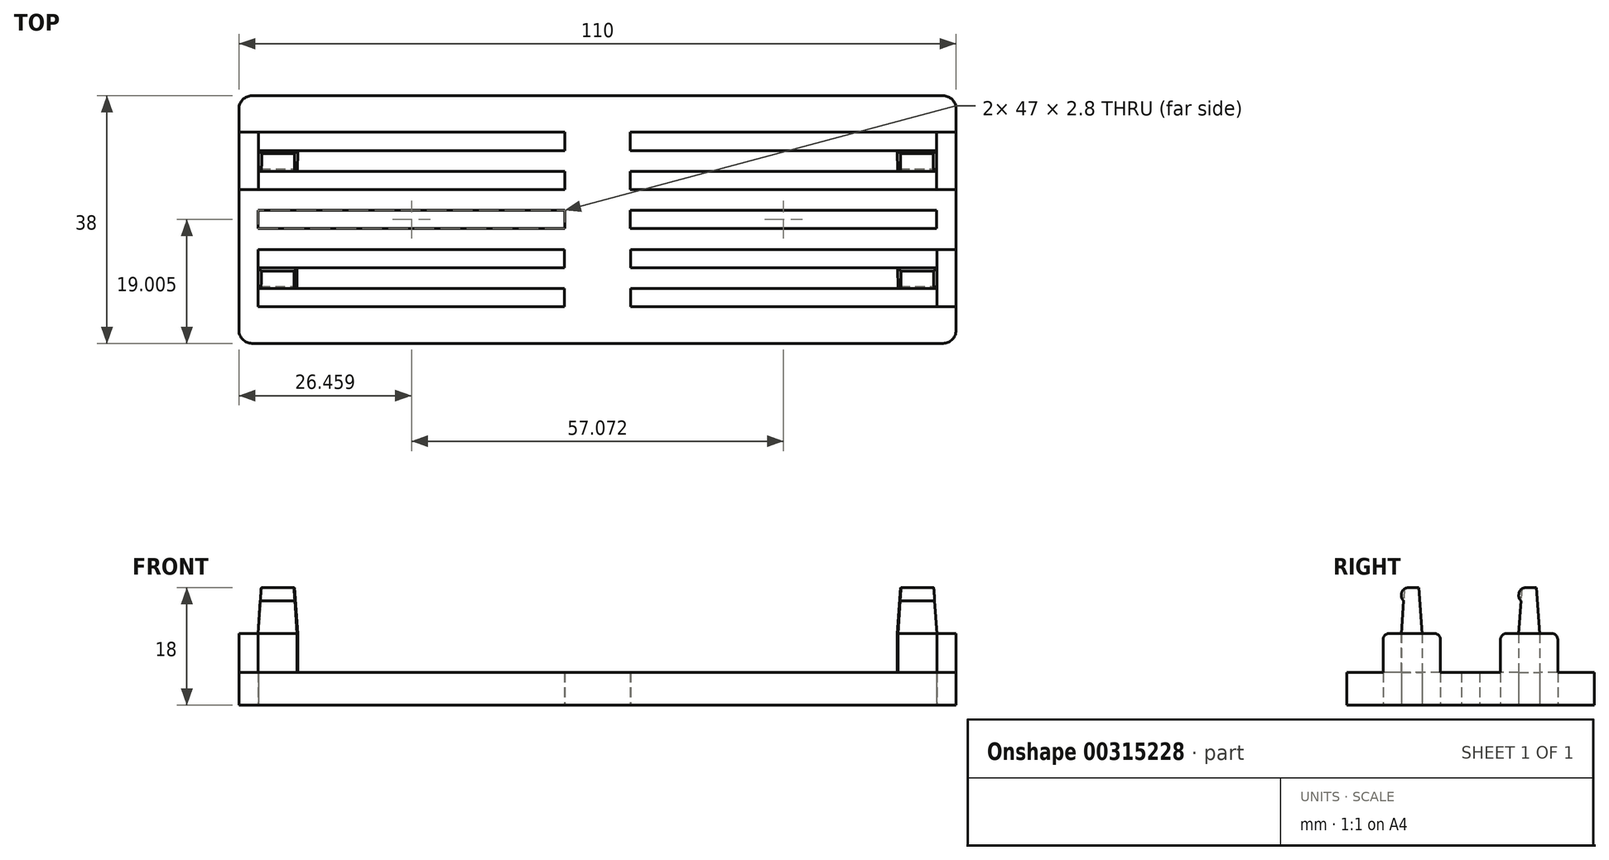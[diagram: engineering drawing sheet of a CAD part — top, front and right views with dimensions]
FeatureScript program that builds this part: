
annotation { "Feature Type Name" : "Feature", "Feature Type Description" : "" }
export const myFeature = defineFeature(function(context is Context, id is Id, definition is map)
    precondition{}
    {
        {
            var Q0;
            Q0=qCreatedBy(makeId("Top.planeOp"),FACE);
            var sketch = newSketch(context, id + "F0", { "sketchPlane" : qUnion([Q0])});
            skLineSegment(sketch, "E0.bottom", {"start": v(-62.65, 12.42) * mm, "end": v(47.35, 12.42) * mm});
            skLineSegment(sketch, "E0.top", {"start": v(-62.65, -25.58) * mm, "end": v(47.35, -25.58) * mm});
            skLineSegment(sketch, "E0.left", {"start": v(-62.65, 12.42) * mm, "end": v(-62.65, -25.58) * mm});
            skLineSegment(sketch, "E0.right", {"start": v(47.35, 12.42) * mm, "end": v(47.35, -25.58) * mm});
            skPoint(sketch, "E1", {"position": v(-7.65, 12.42) * mm});
            skLineSegment(sketch, "E2.bottom", {"start": v(-59.65, 6.82) * mm, "end": v(-12.65, 6.82) * mm});
            skLineSegment(sketch, "E2.top", {"start": v(-59.65, 4.02) * mm, "end": v(-12.65, 4.02) * mm});
            skLineSegment(sketch, "E2.left", {"start": v(-59.65, 6.82) * mm, "end": v(-59.65, 4.02) * mm});
            skLineSegment(sketch, "E2.right", {"start": v(-12.65, 6.82) * mm, "end": v(-12.65, 4.02) * mm});
            skLineSegment(sketch, "E3.1.0.0", {"start": v(-59.67, 0.82) * mm, "end": v(-59.67, -1.98) * mm});
            skLineSegment(sketch, "E3.1.0.1", {"start": v(-59.67, 0.82) * mm, "end": v(-12.67, 0.82) * mm});
            skLineSegment(sketch, "E3.1.0.2", {"start": v(-59.67, -1.98) * mm, "end": v(-12.67, -1.98) * mm});
            skLineSegment(sketch, "E3.1.0.3", {"start": v(-12.67, 0.82) * mm, "end": v(-12.67, -1.98) * mm});
            skLineSegment(sketch, "E3.2.0.0", {"start": v(-59.7, -5.18) * mm, "end": v(-59.7, -7.98) * mm});
            skLineSegment(sketch, "E3.2.0.1", {"start": v(-59.7, -5.18) * mm, "end": v(-12.7, -5.18) * mm});
            skLineSegment(sketch, "E3.2.0.2", {"start": v(-59.7, -7.98) * mm, "end": v(-12.7, -7.98) * mm});
            skLineSegment(sketch, "E3.2.0.3", {"start": v(-12.7, -5.18) * mm, "end": v(-12.7, -7.98) * mm});
            skLineSegment(sketch, "E3.3.0.0", {"start": v(-59.7, -11.17) * mm, "end": v(-59.7, -13.97) * mm});
            skLineSegment(sketch, "E3.3.0.1", {"start": v(-59.7, -11.17) * mm, "end": v(-12.7, -11.17) * mm});
            skLineSegment(sketch, "E3.3.0.2", {"start": v(-59.7, -13.97) * mm, "end": v(-12.7, -13.97) * mm});
            skLineSegment(sketch, "E3.3.0.3", {"start": v(-12.7, -11.17) * mm, "end": v(-12.7, -13.97) * mm});
            skLineSegment(sketch, "E3.4.0.0", {"start": v(-59.73, -17.17) * mm, "end": v(-59.73, -19.97) * mm});
            skLineSegment(sketch, "E3.4.0.1", {"start": v(-59.73, -17.17) * mm, "end": v(-12.73, -17.17) * mm});
            skLineSegment(sketch, "E3.4.0.2", {"start": v(-59.73, -19.97) * mm, "end": v(-12.73, -19.97) * mm});
            skLineSegment(sketch, "E3.4.0.3", {"start": v(-12.73, -17.17) * mm, "end": v(-12.73, -19.97) * mm});
            skLineSegment(sketch, "E3.direction1", {"start": v(-59.65, 4.02) * mm, "end": v(-59.67, -1.98) * mm, "construction": true});
            skPoint(sketch, "E4", {"position": v(-7.65, -25.58) * mm});
            skLineSegment(sketch, "E5.MirrorCS", {"start": v(44.4, -11.17) * mm, "end": v(44.4, -13.97) * mm});
            skLineSegment(sketch, "E6.MirrorCS", {"start": v(-2.6, -11.17) * mm, "end": v(-2.6, -13.97) * mm});
            skLineSegment(sketch, "E7.MirrorCS", {"start": v(-2.62, -5.18) * mm, "end": v(-2.62, -7.98) * mm});
            skLineSegment(sketch, "E8.MirrorCS", {"start": v(44.35, 6.82) * mm, "end": v(44.35, 4.02) * mm});
            skLineSegment(sketch, "E9.MirrorCS", {"start": v(44.36, 0.82) * mm, "end": v(44.36, -1.98) * mm});
            skLineSegment(sketch, "E10.MirrorCS", {"start": v(-2.64, 0.82) * mm, "end": v(-2.64, -1.98) * mm});
            skLineSegment(sketch, "E11.MirrorCS", {"start": v(44.38, -5.18) * mm, "end": v(44.38, -7.98) * mm});
            skLineSegment(sketch, "E12.MirrorCS", {"start": v(-2.65, 6.82) * mm, "end": v(-2.65, 4.02) * mm});
            skLineSegment(sketch, "E13.MirrorCS", {"start": v(-2.58, -17.17) * mm, "end": v(-2.58, -19.97) * mm});
            skLineSegment(sketch, "E14.MirrorCS", {"start": v(44.42, -17.17) * mm, "end": v(44.42, -19.97) * mm});
            skLineSegment(sketch, "E15.MirrorCS", {"start": v(44.42, -17.17) * mm, "end": v(-2.58, -17.17) * mm});
            skLineSegment(sketch, "E16.MirrorCS", {"start": v(44.35, 4.02) * mm, "end": v(44.36, -1.98) * mm, "construction": true});
            skLineSegment(sketch, "E17.MirrorCS", {"start": v(44.38, -5.18) * mm, "end": v(-2.62, -5.18) * mm});
            skLineSegment(sketch, "E18.MirrorCS", {"start": v(44.4, -11.17) * mm, "end": v(-2.6, -11.17) * mm});
            skLineSegment(sketch, "E19.MirrorCS", {"start": v(44.38, -7.98) * mm, "end": v(-2.62, -7.98) * mm});
            skLineSegment(sketch, "E20.MirrorCS", {"start": v(44.35, 6.82) * mm, "end": v(-2.65, 6.82) * mm});
            skLineSegment(sketch, "E21.MirrorCS", {"start": v(44.35, 4.02) * mm, "end": v(-2.65, 4.02) * mm});
            skLineSegment(sketch, "E22.MirrorCS", {"start": v(44.36, 0.82) * mm, "end": v(-2.64, 0.82) * mm});
            skLineSegment(sketch, "E23.MirrorCS", {"start": v(44.36, -1.98) * mm, "end": v(-2.64, -1.98) * mm});
            skLineSegment(sketch, "E24.MirrorCS", {"start": v(44.42, -19.97) * mm, "end": v(-2.58, -19.97) * mm});
            skLineSegment(sketch, "E25.MirrorCS", {"start": v(44.4, -13.97) * mm, "end": v(-2.6, -13.97) * mm});
            skSolve(sketch);
        }
        {
            var Q0;
            Q0=makeQuery(id+"F0.imprint","IMPRINT",FACE,{"disambiguationData":[TD([[makeQuery(id+"F0.imprint","IMPRINT",EDGE,{"derivedFrom":sQuery(id+"F0.wireOp",EDGE,"E0.bottom")}),-1.0]])]});
            extrude(context, id + "F1", {"entities" : qUnion([Q0]), "depth" : 5 * mm});
        }
        {
            var Q0;
            Q0=makeQuery(id+"F1.opExtrude","SWEPT_EDGE",EDGE,{"disambiguationData":[OSD([sQuery(id+"F0.wireOp",EDGE,"E0.bottom"),sQuery(id+"F0.wireOp",EDGE,"E0.left")])]});
            var Q1;
            Q1=makeQuery(id+"F1.opExtrude","SWEPT_EDGE",EDGE,{"disambiguationData":[OSD([sQuery(id+"F0.wireOp",EDGE,"E0.top"),sQuery(id+"F0.wireOp",EDGE,"E0.left")])]});
            var Q2;
            Q2=makeQuery(id+"F1.opExtrude","SWEPT_EDGE",EDGE,{"disambiguationData":[OSD([sQuery(id+"F0.wireOp",EDGE,"E0.bottom"),sQuery(id+"F0.wireOp",EDGE,"E0.right")])]});
            var Q3;
            Q3=makeQuery(id+"F1.opExtrude","SWEPT_EDGE",EDGE,{"disambiguationData":[OSD([sQuery(id+"F0.wireOp",EDGE,"E0.top"),sQuery(id+"F0.wireOp",EDGE,"E0.right")])]});
            fillet(context, id + "F2", {"entities" : qUnion([Q0, Q1, Q2, Q3]), "radius" : 2 * mm, "tangentPropagation" : true, "allowEdgeOverflow" : false});
        }
        {
            var Q0;
            Q0=makeQuery(id+"F1.opExtrude","CAP_FACE",FACE,{"disambiguationData":[OSD([sQuery(id+"F0.wireOp",EDGE,"E0.bottom"),sQuery(id+"F0.wireOp",EDGE,"E0.top"),sQuery(id+"F0.wireOp",EDGE,"E0.left"),sQuery(id+"F0.wireOp",EDGE,"E0.right"),sQuery(id+"F0.wireOp",EDGE,"E2.bottom"),sQuery(id+"F0.wireOp",EDGE,"E2.top"),sQuery(id+"F0.wireOp",EDGE,"E2.left"),sQuery(id+"F0.wireOp",EDGE,"E2.right"),sQuery(id+"F0.wireOp",EDGE,"E3.1.0.0"),sQuery(id+"F0.wireOp",EDGE,"E3.1.0.1"),sQuery(id+"F0.wireOp",EDGE,"E3.1.0.2"),sQuery(id+"F0.wireOp",EDGE,"E3.1.0.3"),sQuery(id+"F0.wireOp",EDGE,"E3.2.0.0"),sQuery(id+"F0.wireOp",EDGE,"E3.2.0.1"),sQuery(id+"F0.wireOp",EDGE,"E3.2.0.2"),sQuery(id+"F0.wireOp",EDGE,"E3.2.0.3"),sQuery(id+"F0.wireOp",EDGE,"E3.3.0.0"),sQuery(id+"F0.wireOp",EDGE,"E3.3.0.1"),sQuery(id+"F0.wireOp",EDGE,"E3.3.0.2"),sQuery(id+"F0.wireOp",EDGE,"E3.3.0.3"),sQuery(id+"F0.wireOp",EDGE,"E3.4.0.0"),sQuery(id+"F0.wireOp",EDGE,"E3.4.0.1"),sQuery(id+"F0.wireOp",EDGE,"E3.4.0.2"),sQuery(id+"F0.wireOp",EDGE,"E3.4.0.3"),sQuery(id+"F0.wireOp",EDGE,"E5.MirrorCS"),sQuery(id+"F0.wireOp",EDGE,"E6.MirrorCS"),sQuery(id+"F0.wireOp",EDGE,"E7.MirrorCS"),sQuery(id+"F0.wireOp",EDGE,"E8.MirrorCS"),sQuery(id+"F0.wireOp",EDGE,"E9.MirrorCS"),sQuery(id+"F0.wireOp",EDGE,"E10.MirrorCS"),sQuery(id+"F0.wireOp",EDGE,"E11.MirrorCS"),sQuery(id+"F0.wireOp",EDGE,"E12.MirrorCS"),sQuery(id+"F0.wireOp",EDGE,"E13.MirrorCS"),sQuery(id+"F0.wireOp",EDGE,"E14.MirrorCS"),sQuery(id+"F0.wireOp",EDGE,"E15.MirrorCS"),sQuery(id+"F0.wireOp",EDGE,"E17.MirrorCS"),sQuery(id+"F0.wireOp",EDGE,"E18.MirrorCS"),sQuery(id+"F0.wireOp",EDGE,"E19.MirrorCS"),sQuery(id+"F0.wireOp",EDGE,"E20.MirrorCS"),sQuery(id+"F0.wireOp",EDGE,"E21.MirrorCS"),sQuery(id+"F0.wireOp",EDGE,"E22.MirrorCS"),sQuery(id+"F0.wireOp",EDGE,"E23.MirrorCS"),sQuery(id+"F0.wireOp",EDGE,"E24.MirrorCS"),sQuery(id+"F0.wireOp",EDGE,"E25.MirrorCS")])],"isStart":false});
            var sketch = newSketch(context, id + "F3", { "sketchPlane" : qUnion([Q0])});
            skLineSegment(sketch, "E26", {"start": v(-59.65, 6.82) * mm, "end": v(-62.65, 6.82) * mm});
            skLineSegment(sketch, "E27", {"start": v(-59.67, -1.98) * mm, "end": v(-62.65, -1.98) * mm});
            skLineSegment(sketch, "E28", {"start": v(-59.67, 0.82) * mm, "end": v(-59.65, 4.02) * mm});
            skLineSegment(sketch, "E29.1.0.0", {"start": v(-53.67, 0.82) * mm, "end": v(-53.65, 4.02) * mm});
            skLineSegment(sketch, "E30.1.0.1", {"start": v(-53.74, -17.17) * mm, "end": v(-53.72, -13.97) * mm});
            skLineSegment(sketch, "E30.1.0.2", {"start": v(-59.74, -17.17) * mm, "end": v(-59.72, -13.97) * mm});
            skLineSegment(sketch, "E30.1.0.3", {"start": v(-59.74, -19.97) * mm, "end": v(-62.72, -19.97) * mm});
            skLineSegment(sketch, "E30.1.0.4", {"start": v(-59.72, -11.17) * mm, "end": v(-62.72, -11.17) * mm});
            skPoint(sketch, "E31", {"position": v(-7.65, 12.42) * mm});
            skPoint(sketch, "E32", {"position": v(-7.65, -25.58) * mm});
            skLineSegment(sketch, "E33", {"start": v(-7.65, 12.42) * mm, "end": v(-7.65, -25.58) * mm});
            skLineSegment(sketch, "E34.MirrorCS", {"start": v(44.35, 6.82) * mm, "end": v(47.35, 6.82) * mm});
            skLineSegment(sketch, "E35.MirrorCS", {"start": v(44.36, -1.98) * mm, "end": v(47.35, -1.98) * mm});
            skLineSegment(sketch, "E36.MirrorCS", {"start": v(44.36, 0.82) * mm, "end": v(44.35, 4.02) * mm});
            skLineSegment(sketch, "E37.MirrorCS", {"start": v(38.36, 0.82) * mm, "end": v(38.35, 4.02) * mm});
            skLineSegment(sketch, "E38.MirrorCS", {"start": v(38.43, -17.17) * mm, "end": v(38.4, -13.97) * mm});
            skLineSegment(sketch, "E39", {"start": v(-59.73, -17.17) * mm, "end": v(-59.7, -13.97) * mm});
            skLineSegment(sketch, "E40", {"start": v(-62.72, -11.17) * mm, "end": v(-59.7, -11.17) * mm});
            skLineSegment(sketch, "E41", {"start": v(-62.72, -19.97) * mm, "end": v(-59.73, -19.97) * mm});
            skLineSegment(sketch, "E42", {"start": v(44.4, -11.17) * mm, "end": v(47.35, -11.17) * mm});
            skLineSegment(sketch, "E43", {"start": v(44.42, -19.97) * mm, "end": v(47.35, -19.97) * mm});
            skLineSegment(sketch, "E44", {"start": v(44.42, -17.17) * mm, "end": v(44.4, -13.97) * mm});
            skSolve(sketch);
        }
        {
            var Q0;
            {var subQ0=sQuery(id+"F3.wireOp",EDGE,"E26");Q0=makeQuery(id+"F3.imprint","IMPRINT",FACE,{"disambiguationData":[TD([[makeQuery(id+"F3.imprint","IMPRINT",EDGE,{"derivedFrom":subQ0}),1.0]])]});}
            var Q1;
            {var subQ0=sQuery(id+"F3.wireOp",EDGE,"E28");Q1=makeQuery(id+"F3.imprint","IMPRINT",FACE,{"disambiguationData":[TD([[makeQuery(id+"F3.imprint","IMPRINT",EDGE,{"derivedFrom":subQ0}),-1.0]])]});}
            var Q2;
            {var subQ0=sQuery(id+"F3.wireOp",EDGE,"E30.1.0.1");Q2=makeQuery(id+"F3.imprint","IMPRINT",FACE,{"disambiguationData":[TD([[makeQuery(id+"F3.imprint","IMPRINT",EDGE,{"derivedFrom":subQ0}),1.0]])]});}
            var Q3;
            {var subQ4=sQuery(id+"F3.wireOp",EDGE,"E30.1.0.3");Q3=makeQuery(id+"F3.imprint","IMPRINT",FACE,{"disambiguationData":[TD([[makeQuery(id+"F3.imprint","IMPRINT",EDGE,{"derivedFrom":subQ4}),-1.0]])]});}
            var Q4;
            {var subQ0=sQuery(id+"F3.wireOp",EDGE,"E38.MirrorCS");Q4=makeQuery(id+"F3.imprint","IMPRINT",FACE,{"disambiguationData":[TD([[makeQuery(id+"F3.imprint","IMPRINT",EDGE,{"derivedFrom":subQ0}),-1.0]])]});}
            var Q5;
            {var subQ0=sQuery(id+"F3.wireOp",EDGE,"E42");Q5=makeQuery(id+"F3.imprint","IMPRINT",FACE,{"disambiguationData":[TD([[makeQuery(id+"F3.imprint","IMPRINT",EDGE,{"derivedFrom":subQ0}),-1.0]])]});}
            var Q6;
            {var subQ0=sQuery(id+"F3.wireOp",EDGE,"E36.MirrorCS");Q6=makeQuery(id+"F3.imprint","IMPRINT",FACE,{"disambiguationData":[TD([[makeQuery(id+"F3.imprint","IMPRINT",EDGE,{"derivedFrom":subQ0}),1.0]])]});}
            var Q7;
            {var subQ0=sQuery(id+"F3.wireOp",EDGE,"E34.MirrorCS");Q7=makeQuery(id+"F3.imprint","IMPRINT",FACE,{"disambiguationData":[TD([[makeQuery(id+"F3.imprint","IMPRINT",EDGE,{"derivedFrom":subQ0}),-1.0]])]});}
            extrude(context, id + "F4", {"entities" : qUnion([Q0, Q1, Q2, Q3, Q4, Q5, Q6, Q7]), "operationType" : NewBodyOperationType.ADD, "depth" : 6 * mm});
        }
        {
            var Q0;
            Q0=makeQuery(id+"F4.opExtrude","CAP_EDGE",EDGE,{"disambiguationData":[OSD([sQuery(id+"F3.wireOp",EDGE,"E26")])],"isStart":false});
            var Q1;
            Q1=makeQuery(id+"F4.opExtrude","CAP_EDGE",EDGE,{"disambiguationData":[OSD([sQuery(id+"F3.wireOp",EDGE,"E27")])],"isStart":false});
            var Q2;
            Q2=makeQuery(id+"F4.opExtrude","CAP_EDGE",EDGE,{"disambiguationData":[OSD([sQuery(id+"F3.wireOp",EDGE,"E40")])],"isStart":false});
            var Q3;
            Q3=makeQuery(id+"F4.opExtrude","CAP_EDGE",EDGE,{"disambiguationData":[OSD([sQuery(id+"F3.wireOp",EDGE,"E30.1.0.3")])],"isStart":false});
            var Q4;
            Q4=makeQuery(id+"F4.opExtrude","CAP_EDGE",EDGE,{"disambiguationData":[OSD([sQuery(id+"F3.wireOp",EDGE,"E43")])],"isStart":false});
            var Q5;
            Q5=makeQuery(id+"F4.opExtrude","CAP_EDGE",EDGE,{"disambiguationData":[OSD([sQuery(id+"F3.wireOp",EDGE,"E42")])],"isStart":false});
            var Q6;
            Q6=makeQuery(id+"F4.opExtrude","CAP_EDGE",EDGE,{"disambiguationData":[OSD([sQuery(id+"F3.wireOp",EDGE,"E35.MirrorCS")])],"isStart":false});
            var Q7;
            Q7=makeQuery(id+"F4.opExtrude","CAP_EDGE",EDGE,{"disambiguationData":[OSD([sQuery(id+"F3.wireOp",EDGE,"E34.MirrorCS")])],"isStart":false});
            var Q8;
            Q8=makeQuery(id+"F4.opExtrude","CAP_EDGE",EDGE,{"disambiguationData":[OSD([sQuery(id+"F3.wireOp",EDGE,"E26")])],"isStart":true});
            var Q9;
            Q9=makeQuery(id+"F4.opExtrude","CAP_EDGE",EDGE,{"disambiguationData":[OSD([sQuery(id+"F3.wireOp",EDGE,"E40")])],"isStart":true});
            var Q10;
            Q10=makeQuery(id+"F4.opExtrude","CAP_EDGE",EDGE,{"disambiguationData":[OSD([sQuery(id+"F3.wireOp",EDGE,"E42")])],"isStart":true});
            var Q11;
            Q11=makeQuery(id+"F4.opExtrude","CAP_EDGE",EDGE,{"disambiguationData":[OSD([sQuery(id+"F3.wireOp",EDGE,"E34.MirrorCS")])],"isStart":true});
            var Q12;
            Q12=makeQuery(id+"F4.opExtrude","CAP_EDGE",EDGE,{"disambiguationData":[OSD([sQuery(id+"F3.wireOp",EDGE,"E37.MirrorCS")])],"isStart":true});
            var Q13;
            Q13=makeQuery(id+"F4.opExtrude","CAP_EDGE",EDGE,{"disambiguationData":[OSD([sQuery(id+"F3.wireOp",EDGE,"E38.MirrorCS")])],"isStart":true});
            var Q14;
            Q14=makeQuery(id+"F4.opExtrude","CAP_EDGE",EDGE,{"disambiguationData":[OSD([sQuery(id+"F3.wireOp",EDGE,"E29.1.0.0")])],"isStart":true});
            var Q15;
            Q15=makeQuery(id+"F4.opExtrude","CAP_EDGE",EDGE,{"disambiguationData":[OSD([sQuery(id+"F3.wireOp",EDGE,"E27")])],"isStart":true});
            var Q16;
            Q16=makeQuery(id+"F4.opExtrude","CAP_EDGE",EDGE,{"disambiguationData":[OSD([sQuery(id+"F3.wireOp",EDGE,"E30.1.0.1")])],"isStart":true});
            var Q17;
            Q17=makeQuery(id+"F4.opExtrude","CAP_EDGE",EDGE,{"disambiguationData":[OSD([sQuery(id+"F3.wireOp",EDGE,"E30.1.0.3")])],"isStart":true});
            var Q18;
            Q18=makeQuery(id+"F4.opExtrude","CAP_EDGE",EDGE,{"disambiguationData":[OSD([sQuery(id+"F3.wireOp",EDGE,"E43")])],"isStart":true});
            var Q19;
            Q19=makeQuery(id+"F4.opExtrude","CAP_EDGE",EDGE,{"disambiguationData":[OSD([sQuery(id+"F3.wireOp",EDGE,"E35.MirrorCS")])],"isStart":true});
            fillet(context, id + "F5", {"entities" : qUnion([Q0, Q1, Q2, Q3, Q4, Q5, Q6, Q7, Q8, Q9, Q10, Q11, Q12, Q13, Q14, Q15, Q16, Q17, Q18, Q19]), "radius" : 1 * mm, "tangentPropagation" : true, "allowEdgeOverflow" : false});
        }
        {
            var Q0;
            Q0=makeQuery(id+"F4.opExtrude","CAP_FACE",FACE,{"disambiguationData":[OSD([sQuery(id+"F0.wireOp",EDGE,"E0.left"),sQuery(id+"F0.wireOp",EDGE,"E2.top"),sQuery(id+"F0.wireOp",EDGE,"E2.left"),sQuery(id+"F0.wireOp",EDGE,"E3.1.0.0"),sQuery(id+"F0.wireOp",EDGE,"E3.1.0.1"),sQuery(id+"F3.wireOp",EDGE,"E26"),sQuery(id+"F3.wireOp",EDGE,"E27"),sQuery(id+"F3.wireOp",EDGE,"E29.1.0.0")])],"isStart":false});
            var sketch = newSketch(context, id + "F6", { "sketchPlane" : qUnion([Q0])});
            skLineSegment(sketch, "E45", {"start": v(-59.67, 0.82) * mm, "end": v(-59.65, 4.02) * mm});
            skSolve(sketch);
        }
        {
            var Q0;
            Q0=makeQuery(id+"F4.opExtrude","CAP_FACE",FACE,{"disambiguationData":[OSD([sQuery(id+"F0.wireOp",EDGE,"E0.left"),sQuery(id+"F0.wireOp",EDGE,"E3.3.0.0"),sQuery(id+"F0.wireOp",EDGE,"E3.3.0.2"),sQuery(id+"F0.wireOp",EDGE,"E3.4.0.0"),sQuery(id+"F0.wireOp",EDGE,"E3.4.0.1"),sQuery(id+"F3.wireOp",EDGE,"E30.1.0.3"),sQuery(id+"F3.wireOp",EDGE,"E30.1.0.1"),sQuery(id+"F3.wireOp",EDGE,"E40"),sQuery(id+"F3.wireOp",EDGE,"E41")])],"isStart":false});
            var sketch = newSketch(context, id + "F7", { "sketchPlane" : qUnion([Q0])});
            skLineSegment(sketch, "E46", {"start": v(-59.73, -17.17) * mm, "end": v(-59.7, -13.97) * mm});
            skSolve(sketch);
        }
        {
            var Q0;
            Q0=makeQuery(id+"F4.opExtrude","CAP_FACE",FACE,{"disambiguationData":[OSD([sQuery(id+"F0.wireOp",EDGE,"E0.right"),sQuery(id+"F0.wireOp",EDGE,"E8.MirrorCS"),sQuery(id+"F0.wireOp",EDGE,"E9.MirrorCS"),sQuery(id+"F0.wireOp",EDGE,"E21.MirrorCS"),sQuery(id+"F0.wireOp",EDGE,"E22.MirrorCS"),sQuery(id+"F3.wireOp",EDGE,"E34.MirrorCS"),sQuery(id+"F3.wireOp",EDGE,"E35.MirrorCS"),sQuery(id+"F3.wireOp",EDGE,"E37.MirrorCS")])],"isStart":false});
            var sketch = newSketch(context, id + "F8", { "sketchPlane" : qUnion([Q0])});
            skLineSegment(sketch, "E47", {"start": v(44.36, 0.82) * mm, "end": v(44.35, 4.02) * mm});
            skSolve(sketch);
        }
        {
            var Q0;
            Q0=makeQuery(id+"F4.opExtrude","CAP_FACE",FACE,{"disambiguationData":[OSD([sQuery(id+"F0.wireOp",EDGE,"E0.right"),sQuery(id+"F0.wireOp",EDGE,"E5.MirrorCS"),sQuery(id+"F0.wireOp",EDGE,"E14.MirrorCS"),sQuery(id+"F0.wireOp",EDGE,"E15.MirrorCS"),sQuery(id+"F0.wireOp",EDGE,"E25.MirrorCS"),sQuery(id+"F3.wireOp",EDGE,"E38.MirrorCS"),sQuery(id+"F3.wireOp",EDGE,"E42"),sQuery(id+"F3.wireOp",EDGE,"E43")])],"isStart":false});
            var sketch = newSketch(context, id + "F9", { "sketchPlane" : qUnion([Q0])});
            skLineSegment(sketch, "E48", {"start": v(44.42, -17.17) * mm, "end": v(44.4, -13.97) * mm});
            skSolve(sketch);
        }
        {
            var Q0;
            Q0=makeQuery(id+"F6.imprint","IMPRINT",FACE,{"disambiguationData":[TD([[makeQuery(id+"F6.imprint","IMPRINT",EDGE,{"derivedFrom":sQuery(id+"F6.wireOp",EDGE,"E45")}),-1.0]])]});
            var Q1;
            Q1=makeQuery(id+"F7.imprint","IMPRINT",FACE,{"disambiguationData":[TD([[makeQuery(id+"F7.imprint","IMPRINT",EDGE,{"derivedFrom":sQuery(id+"F7.wireOp",EDGE,"E46")}),-1.0]])]});
            var Q2;
            Q2=makeQuery(id+"F9.imprint","IMPRINT",FACE,{"disambiguationData":[TD([[makeQuery(id+"F9.imprint","IMPRINT",EDGE,{"derivedFrom":sQuery(id+"F9.wireOp",EDGE,"E48")}),1.0]])]});
            var Q3;
            Q3=makeQuery(id+"F8.imprint","IMPRINT",FACE,{"disambiguationData":[TD([[makeQuery(id+"F8.imprint","IMPRINT",EDGE,{"derivedFrom":sQuery(id+"F8.wireOp",EDGE,"E47")}),1.0]])]});
            extrude(context, id + "F10", {"entities" : qUnion([Q0, Q1, Q2, Q3]), "operationType" : NewBodyOperationType.ADD, "depth" : 7 * mm, "hasDraft" : true, "draftAngle" : 4 * degree, "draftPullDirection" : true});
        }
        {
            var Q0;
            Q0=makeQuery(id+"F10.opExtrude","SWEPT_FACE",FACE,{"disambiguationData":[OSD([sQuery(id+"F0.wireOp",EDGE,"E3.1.0.1")])]});
            var sketch = newSketch(context, id + "F11", { "sketchPlane" : qUnion([Q0])});
            skLineSegment(sketch, "E49", {"start": v(-59.32, 16.05) * mm, "end": v(-54.02, 16.05) * mm});
            skSolve(sketch);
        }
        {
            var Q0;
            Q0=makeQuery(id+"F10.opExtrude","SWEPT_FACE",FACE,{"disambiguationData":[OSD([sQuery(id+"F0.wireOp",EDGE,"E3.4.0.1")])]});
            var sketch = newSketch(context, id + "F12", { "sketchPlane" : qUnion([Q0])});
            skLineSegment(sketch, "E50", {"start": v(-59.37, 14.8) * mm, "end": v(-54.08, 14.8) * mm});
            skSolve(sketch);
        }
        {
            var Q0;
            Q0=makeQuery(id+"F10.opExtrude","SWEPT_FACE",FACE,{"disambiguationData":[OSD([sQuery(id+"F0.wireOp",EDGE,"E22.MirrorCS")])]});
            var sketch = newSketch(context, id + "F13", { "sketchPlane" : qUnion([Q0])});
            skLineSegment(sketch, "E51", {"start": v(38.71, 16.05) * mm, "end": v(44.01, 16.05) * mm});
            skSolve(sketch);
        }
        {
            var Q0;
            Q0=makeQuery(id+"F10.opExtrude","SWEPT_FACE",FACE,{"disambiguationData":[OSD([sQuery(id+"F0.wireOp",EDGE,"E15.MirrorCS")])]});
            var sketch = newSketch(context, id + "F14", { "sketchPlane" : qUnion([Q0])});
            skLineSegment(sketch, "E52", {"start": v(38.77, 14.8) * mm, "end": v(44.07, 14.8) * mm});
            skSolve(sketch);
        }
        {
            var Q0;
            {var subQ0=sQuery(id+"F11.wireOp",EDGE,"E49");Q0=makeQuery(id+"F11.imprint","IMPRINT",FACE,{"disambiguationData":[TD([[makeQuery(id+"F11.imprint","IMPRINT",EDGE,{"derivedFrom":subQ0}),1.0]])]});}
            var Q1;
            {var subQ0=sQuery(id+"F12.wireOp",EDGE,"E50");Q1=makeQuery(id+"F12.imprint","IMPRINT",FACE,{"disambiguationData":[TD([[makeQuery(id+"F12.imprint","IMPRINT",EDGE,{"derivedFrom":subQ0}),1.0]])]});}
            var Q2;
            {var subQ0=sQuery(id+"F13.wireOp",EDGE,"E51");Q2=makeQuery(id+"F13.imprint","IMPRINT",FACE,{"disambiguationData":[TD([[makeQuery(id+"F13.imprint","IMPRINT",EDGE,{"derivedFrom":subQ0}),1.0]])]});}
            var Q3;
            {var subQ0=sQuery(id+"F14.wireOp",EDGE,"E52");Q3=makeQuery(id+"F14.imprint","IMPRINT",FACE,{"disambiguationData":[TD([[makeQuery(id+"F14.imprint","IMPRINT",EDGE,{"derivedFrom":subQ0}),1.0]])]});}
            extrude(context, id + "F15", {"entities" : qUnion([Q0, Q1, Q2, Q3]), "operationType" : NewBodyOperationType.ADD, "depth" : 0.4 * mm});
        }
        {
            var Q0;
            Q0=makeQuery(id+"F15.opExtrude","CAP_EDGE",EDGE,{"disambiguationData":[OSD([sQuery(id+"F12.wireOp",EDGE,"E50")])],"isStart":false});
            var Q1;
            Q1=makeQuery(id+"F15.opExtrude","CAP_EDGE",EDGE,{"disambiguationData":[OSD([sQuery(id+"F0.wireOp",EDGE,"E3.4.0.1")])],"isStart":false});
            var Q2;
            Q2=makeQuery(id+"F15.opExtrude","CAP_EDGE",EDGE,{"disambiguationData":[OSD([sQuery(id+"F0.wireOp",EDGE,"E3.1.0.1")])],"isStart":false});
            var Q3;
            Q3=makeQuery(id+"F15.opExtrude","CAP_EDGE",EDGE,{"disambiguationData":[OSD([sQuery(id+"F11.wireOp",EDGE,"E49")])],"isStart":false});
            var Q4;
            Q4=makeQuery(id+"F15.opExtrude","CAP_EDGE",EDGE,{"disambiguationData":[OSD([sQuery(id+"F13.wireOp",EDGE,"E51")])],"isStart":false});
            var Q5;
            Q5=makeQuery(id+"F15.opExtrude","CAP_EDGE",EDGE,{"disambiguationData":[OSD([sQuery(id+"F0.wireOp",EDGE,"E22.MirrorCS")])],"isStart":false});
            var Q6;
            Q6=makeQuery(id+"F15.opExtrude","CAP_EDGE",EDGE,{"disambiguationData":[OSD([sQuery(id+"F0.wireOp",EDGE,"E15.MirrorCS")])],"isStart":false});
            var Q7;
            Q7=makeQuery(id+"F15.opExtrude","CAP_EDGE",EDGE,{"disambiguationData":[OSD([sQuery(id+"F14.wireOp",EDGE,"E52")])],"isStart":false});
            fillet(context, id + "F16", {"entities" : qUnion([Q0, Q1, Q2, Q3, Q4, Q5, Q6, Q7]), "radius" : 1 * mm, "tangentPropagation" : true, "allowEdgeOverflow" : false});
        }
    });
